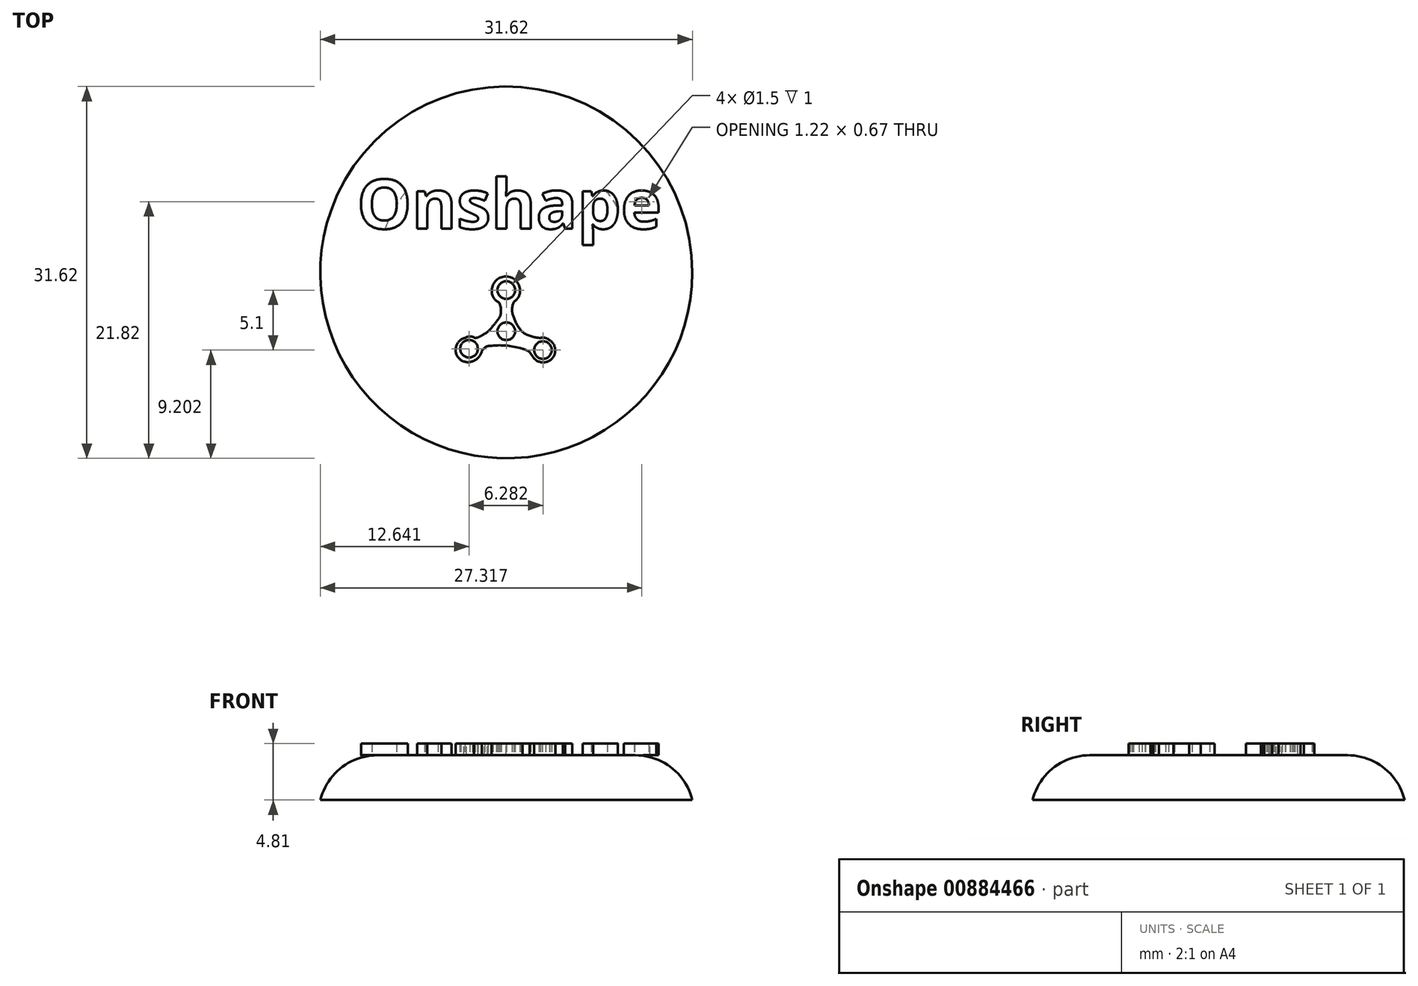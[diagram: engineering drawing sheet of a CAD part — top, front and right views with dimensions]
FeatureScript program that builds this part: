
annotation { "Feature Type Name" : "Feature", "Feature Type Description" : "" }
export const myFeature = defineFeature(function(context is Context, id is Id, definition is map)
    precondition{}
    {
        {
            var Q0;
            Q0=qCreatedBy(makeId("Top.planeOp"),FACE);
            var sketch = newSketch(context, id + "F0", { "sketchPlane" : qUnion([Q0])});
            skCircle(sketch, "E0", {"center": v(0, 0) * mm, "radius": 15.8 * mm});
            skSolve(sketch);
        }
        {
            var Q0;
            Q0=makeQuery(id+"F0.imprint","IMPRINT",FACE,{"disambiguationData":[TD([[makeQuery(id+"F0.imprint","IMPRINT",EDGE,{"derivedFrom":sQuery(id+"F0.wireOp",EDGE,"E0")}),1.0]])]});
            extrude(context, id + "F1", {"entities" : qUnion([Q0]), "depth" : 3.81 * mm, "offsetDistance" : 25 * mm});
        }
        {
            var Q0;
            Q0=makeQuery(id+"F1.opExtrude","CAP_EDGE",EDGE,{"disambiguationData":[OSD([sQuery(id+"F0.wireOp",EDGE,"E0")])],"isStart":false});
            fillet(context, id + "F2", {"entities" : qUnion([Q0]), "radius" : 5 * mm, "tangentPropagation" : true, "allowEdgeOverflow" : false});
        }
        {
            var Q0;
            Q0=makeQuery(id+"F1.opExtrude","CAP_FACE",FACE,{"disambiguationData":[OSD([sQuery(id+"F0.wireOp",EDGE,"E0")])],"isStart":false});
            var sketch = newSketch(context, id + "F3", { "sketchPlane" : qUnion([Q0])});
            skText(sketch, "E1", { "text": "Onshape", "fontName": "OpenSans-Bold.ttf"});
            const initialGuessF3  = {"E1": [-0.01269, 0.00372, 1, 0, 0.0042]};
            skSetInitialGuess(sketch, initialGuessF3);
            skSolve(sketch);
        }
        {
            var Q0;
            Q0 = qSketchRegion(id + "F3", true);
            extrude(context, id + "F4", {"entities" : qUnion([Q0]), "operationType" : NewBodyOperationType.ADD, "depth" : 1 * mm, "offsetDistance" : 25 * mm});
        }
        {
            var Q0;
            {var subQ17=sQuery(id+"F3.wireOp",EDGE,"E1.sketch_text.stroke-0");var subQ18=sQuery(id+"F0.wireOp",EDGE,"E0");Q0=makeQuery(id+"F4.boolean.opBoolean","SPLIT",FACE,{"disambiguationData":[TD([makeQuery(id+"F4.opExtrude","SWEPT_FACE",FACE,{"disambiguationData":[OSD([subQ17])]})])],"derivedFrom":makeQuery(id+"F1.opExtrude","CAP_FACE",FACE,{"disambiguationData":[OSD([subQ18])],"isStart":false})});}
            var sketch = newSketch(context, id + "F5", { "sketchPlane" : qUnion([Q0])});
            skLineSegment(sketch, "E2", {"start": v(0, 0) * mm, "end": v(0, -10.95) * mm, "construction": true});
            skSolve(sketch);
        }
        {
            var Q0;
            {var subQ23=sQuery(id+"F3.wireOp",EDGE,"E1.sketch_text.stroke-0");Q0=makeQuery(id+"F5.imprint","IMPRINT",FACE,{"disambiguationData":[TD([[makeQuery(id+"F5.imprint","IMPRINT",EDGE,{"derivedFrom":makeQuery(id+"F4.opExtrude","CAP_EDGE",EDGE,{"disambiguationData":[OSD([subQ23])],"isStart":true})}),1.0]])]});}
            var sketch = newSketch(context, id + "F6", { "sketchPlane" : qUnion([Q0])});
            skCircle(sketch, "E3", {"center": v(0, -5) * mm, "radius": 0.75 * mm});
            skCircle(sketch, "E4", {"center": v(-3.17, -6.5) * mm, "radius": 0.75 * mm});
            skCircle(sketch, "E5", {"center": v(0, -1.5) * mm, "radius": 0.75 * mm});
            skCircle(sketch, "E6", {"center": v(3.11, -6.6) * mm, "radius": 0.75 * mm});
            skArc(sketch, "E7", {"start": v(1.17, -1.5) * mm, "mid": v(-0.03, -0.34) * mm, "end": v(-1.23, -1.5) * mm});
            skArc(sketch, "E8", {"start": v(-1.23, -1.5) * mm, "mid": v(-1.1, -2.12) * mm, "end": v(-0.64, -2.54) * mm});
            skArc(sketch, "E9", {"start": v(0.65, -2.5) * mm, "mid": v(1.05, -2.08) * mm, "end": v(1.17, -1.5) * mm});
            skArc(sketch, "E10", {"start": v(-3.5, -5.57) * mm, "mid": v(-4.24, -6.97) * mm, "end": v(-2.76, -7.51) * mm});
            skArc(sketch, "E11", {"start": v(-2.66, -5.57) * mm, "mid": v(-3.09, -5.46) * mm, "end": v(-3.5, -5.57) * mm});
            skArc(sketch, "E12", {"start": v(-2.66, -5.57) * mm, "mid": v(-2.36, -5.51) * mm, "end": v(-2.1, -5.36) * mm});
            skArc(sketch, "E13", {"start": v(-2.76, -7.51) * mm, "mid": v(-2.34, -7.22) * mm, "end": v(-2.1, -6.77) * mm});
            skArc(sketch, "E14", {"start": v(-1.25, -6.24) * mm, "mid": v(-1.77, -6.36) * mm, "end": v(-2.1, -6.77) * mm});
            skArc(sketch, "E15", {"start": v(1.37, -6.5) * mm, "mid": v(0.07, -6.23) * mm, "end": v(-1.25, -6.24) * mm});
            skArc(sketch, "E16", {"start": v(1.98, -6.77) * mm, "mid": v(1.69, -6.6) * mm, "end": v(1.37, -6.5) * mm});
            skArc(sketch, "E17", {"start": v(2.37, -7.32) * mm, "mid": v(3.91, -7.3) * mm, "end": v(3.68, -5.77) * mm});
            skArc(sketch, "E18", {"start": v(3.68, -5.77) * mm, "mid": v(3.32, -5.58) * mm, "end": v(2.9, -5.57) * mm});
            skArc(sketch, "E19", {"start": v(0.65, -2.5) * mm, "mid": v(0.49, -3.17) * mm, "end": v(0.65, -3.85) * mm});
            skArc(sketch, "E20", {"start": v(0.65, -3.85) * mm, "mid": v(0.95, -4.5) * mm, "end": v(1.37, -5.08) * mm});
            skArc(sketch, "E21", {"start": v(1.37, -5.08) * mm, "mid": v(2.1, -5.44) * mm, "end": v(2.9, -5.57) * mm});
            skArc(sketch, "E22", {"start": v(1.98, -6.77) * mm, "mid": v(2.17, -7.05) * mm, "end": v(2.37, -7.32) * mm});
            skArc(sketch, "E23", {"start": v(-2.1, -5.36) * mm, "mid": v(-1.54, -5) * mm, "end": v(-1.12, -4.52) * mm});
            skArc(sketch, "E24", {"start": v(-1.12, -4.52) * mm, "mid": v(-0.8, -4.14) * mm, "end": v(-0.53, -3.73) * mm});
            skArc(sketch, "E25", {"start": v(-0.53, -3.73) * mm, "mid": v(-0.45, -3.13) * mm, "end": v(-0.64, -2.54) * mm});
            skSolve(sketch);
        }
        {
            var Q0;
            Q0=makeQuery(id+"F6.imprint","IMPRINT",FACE,{"disambiguationData":[TD([[makeQuery(id+"F6.imprint","IMPRINT",EDGE,{"derivedFrom":sQuery(id+"F6.wireOp",EDGE,"E3")}),-1.0]])]});
            extrude(context, id + "F7", {"entities" : qUnion([Q0]), "operationType" : NewBodyOperationType.ADD, "depth" : 1 * mm, "offsetDistance" : 25 * mm});
        }
    });
